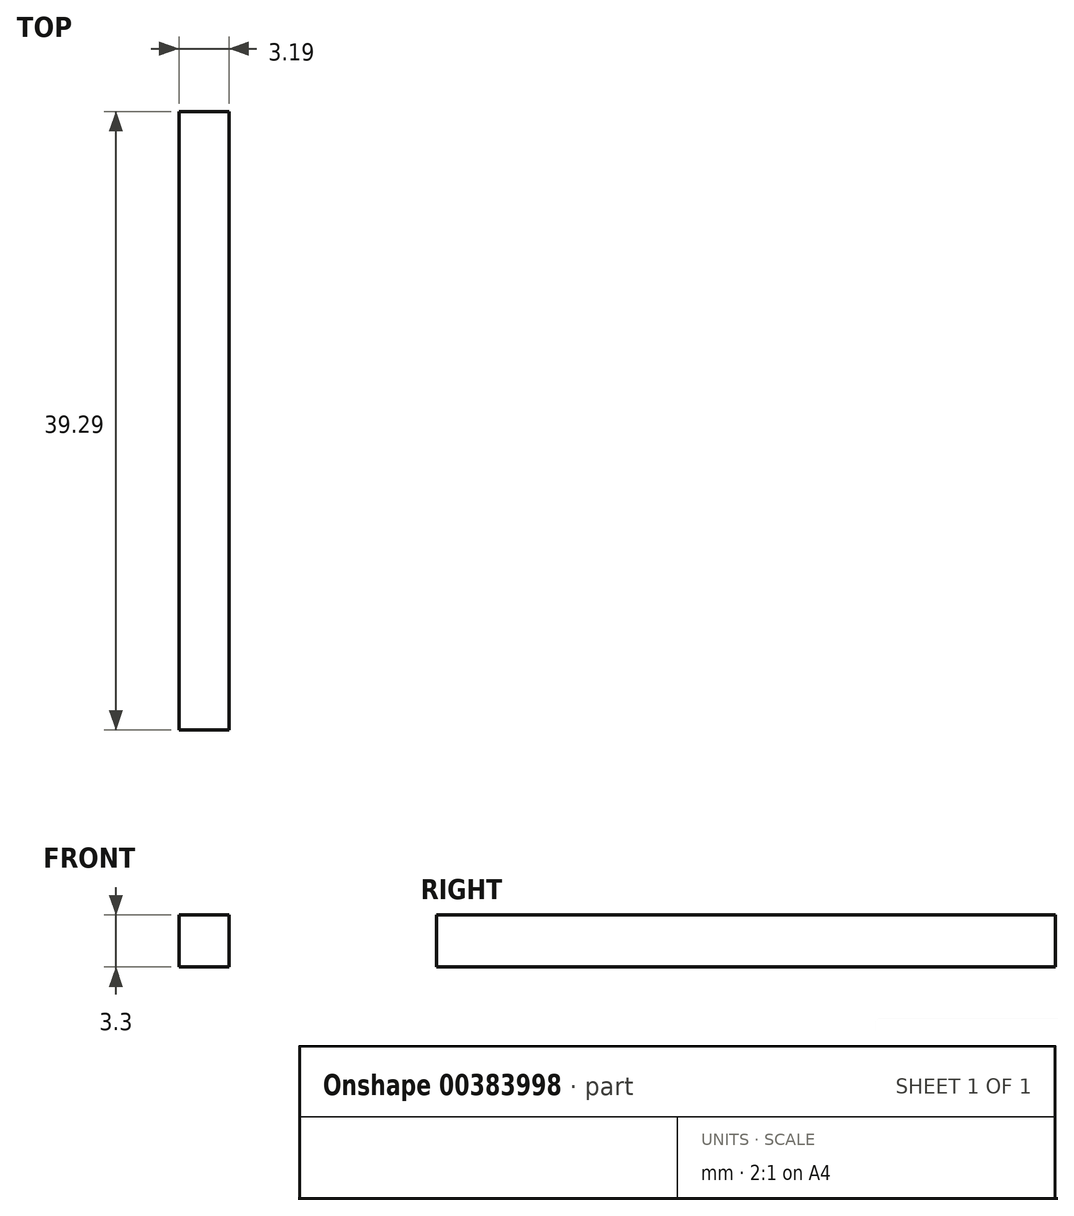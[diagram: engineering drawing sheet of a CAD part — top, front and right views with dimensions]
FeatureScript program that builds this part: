
annotation { "Feature Type Name" : "Feature", "Feature Type Description" : "" }
export const myFeature = defineFeature(function(context is Context, id is Id, definition is map)
    precondition{}
    {
        {
            var Q0;
            Q0=qCreatedBy(makeId("Top.planeOp"),FACE);
            var sketch = newSketch(context, id + "F0", { "sketchPlane" : qUnion([Q0])});
            skLineSegment(sketch, "E0.bottom", {"start": v(0, 0) * mm, "end": v(3.2, 0) * mm});
            skLineSegment(sketch, "E0.top", {"start": v(0, 39.29) * mm, "end": v(3.2, 39.29) * mm});
            skLineSegment(sketch, "E0.left", {"start": v(0, 0) * mm, "end": v(0, 39.29) * mm});
            skLineSegment(sketch, "E0.right", {"start": v(3.2, 0) * mm, "end": v(3.2, 39.29) * mm});
            skSolve(sketch);
        }
        {
            var Q0;
            Q0 = qSketchRegion(id + "F0", true);
            extrude(context, id + "F1", {"entities" : qUnion([Q0]), "depth" : 3.3 * mm, "offsetDistance" : 25.4 * mm});
        }
    });
